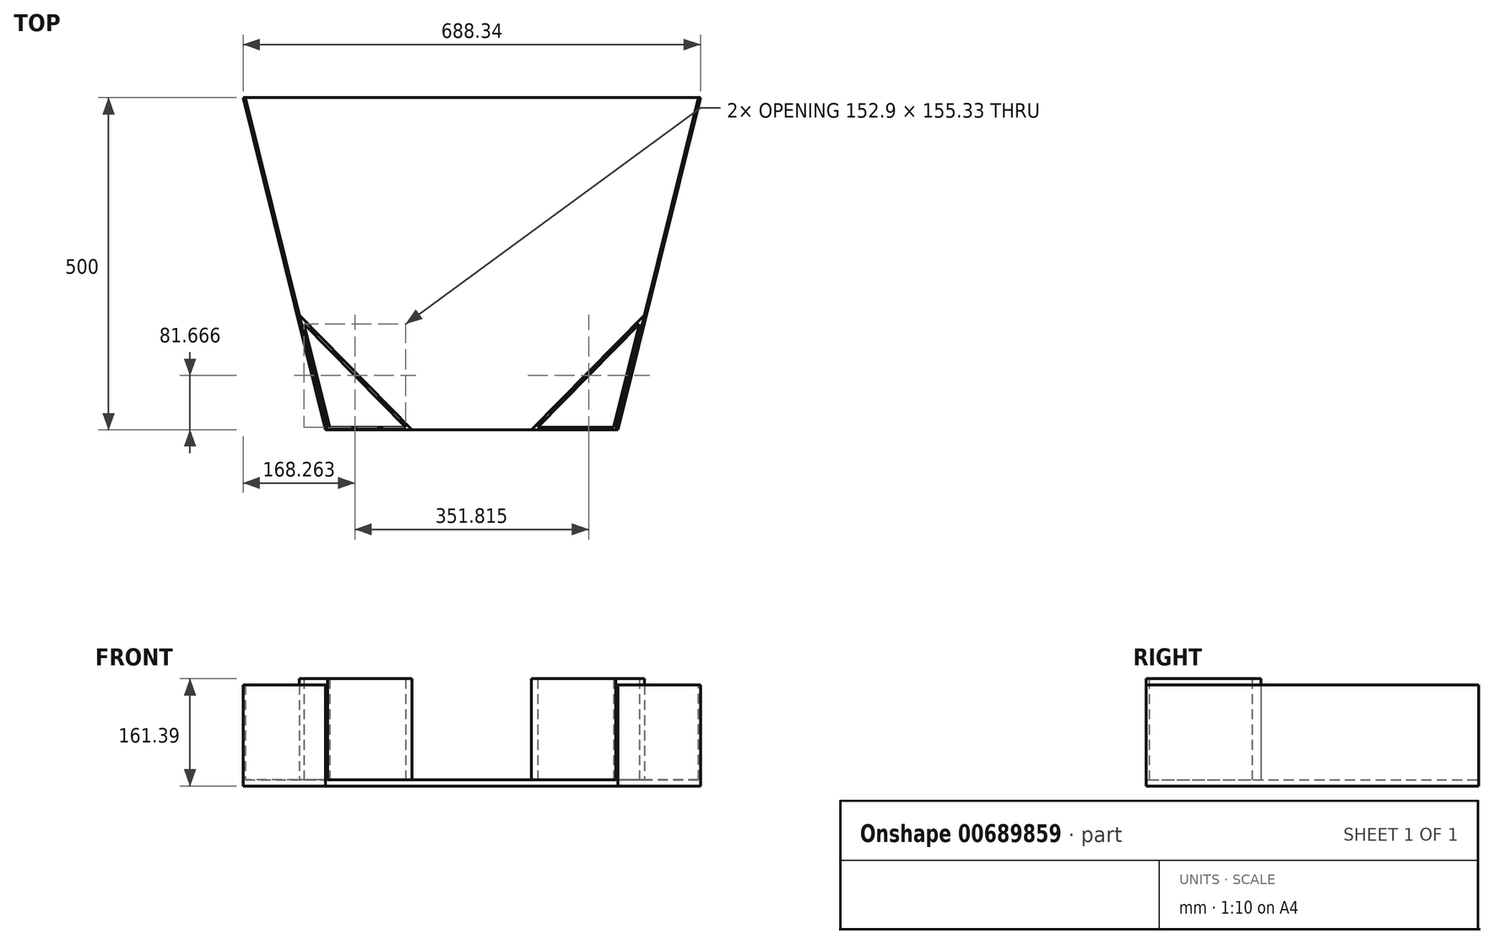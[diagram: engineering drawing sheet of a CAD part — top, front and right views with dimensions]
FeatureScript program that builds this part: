
annotation { "Feature Type Name" : "Feature", "Feature Type Description" : "" }
export const myFeature = defineFeature(function(context is Context, id is Id, definition is map)
    precondition{}
    {
        {
            var Q0;
            Q0=qCreatedBy(makeId("Top.planeOp"),FACE);
            var sketch = newSketch(context, id + "F0", { "sketchPlane" : qUnion([Q0])});
            skLineSegment(sketch, "E0", {"start": v(-344.17, 0) * mm, "end": v(344.17, 0) * mm});
            skLineSegment(sketch, "E1", {"start": v(344.17, 0) * mm, "end": v(220, -500) * mm});
            skLineSegment(sketch, "E2", {"start": v(220, -500) * mm, "end": v(-220, -500) * mm});
            skLineSegment(sketch, "E3", {"start": v(-220, -500) * mm, "end": v(-344.17, 0) * mm});
            skSolve(sketch);
        }
        {
            var Q0;
            Q0 = qSketchRegion(id + "F0", true);
            extrude(context, id + "F1", {"entities" : qUnion([Q0]), "depth" : 152.4 * mm, "offsetDistance" : 25.4 * mm});
        }
        {
            var Q0;
            Q0=makeQuery(id+"F1.opExtrude","CAP_FACE",FACE,{"disambiguationData":[OSD([sQuery(id+"F0.wireOp",EDGE,"E0"),sQuery(id+"F0.wireOp",EDGE,"E1"),sQuery(id+"F0.wireOp",EDGE,"E2"),sQuery(id+"F0.wireOp",EDGE,"E3")])],"isStart":false});
            var sketch = newSketch(context, id + "F2", { "sketchPlane" : qUnion([Q0])});
            skLineSegment(sketch, "E4.0", {"start": v(-216.9, -500) * mm, "end": v(-341.26, 0.72) * mm});
            skLineSegment(sketch, "E5.0", {"start": v(341.26, 0.72) * mm, "end": v(216.9, -500) * mm});
            skLineSegment(sketch, "E6", {"start": v(-341.26, 0.72) * mm, "end": v(341.26, 0.72) * mm});
            skLineSegment(sketch, "E7", {"start": v(-216.9, -500) * mm, "end": v(216.9, -500) * mm});
            skSolve(sketch);
        }
        {
            var Q0;
            Q0 = qSketchRegion(id + "F2", true);
            extrude(context, id + "F3", {"entities" : qUnion([Q0]), "operationType" : NewBodyOperationType.REMOVE, "oppositeDirection" : true, "depth" : 143.4 * mm, "offsetDistance" : 25.4 * mm});
        }
        {
            var Q0;
            Q0=makeQuery(id+"F3.boolean.opBoolean","COPY",FACE,{"derivedFrom":makeQuery(id+"F3.opExtrude","CAP_FACE",FACE,{"disambiguationData":[OSD([sQuery(id+"F2.wireOp",EDGE,"E4.0"),sQuery(id+"F2.wireOp",EDGE,"E5.0"),sQuery(id+"F2.wireOp",EDGE,"E6"),sQuery(id+"F2.wireOp",EDGE,"E7")])],"isStart":false})});
            var sketch = newSketch(context, id + "F4", { "sketchPlane" : qUnion([Q0])});
            skLineSegment(sketch, "E8", {"start": v(216.9, -500) * mm, "end": v(89.9, -500) * mm});
            skLineSegment(sketch, "E9", {"start": v(89.9, -500) * mm, "end": v(259.76, -327.44) * mm});
            skLineSegment(sketch, "E10", {"start": v(259.76, -327.44) * mm, "end": v(216.9, -500) * mm});
            skLineSegment(sketch, "E11", {"start": v(0, -500) * mm, "end": v(0, 0) * mm, "construction": true});
            skLineSegment(sketch, "E12.MirrorCS", {"start": v(-216.9, -500) * mm, "end": v(-89.9, -500) * mm});
            skLineSegment(sketch, "E13.MirrorCS", {"start": v(-259.76, -327.44) * mm, "end": v(-216.9, -500) * mm});
            skLineSegment(sketch, "E14.MirrorCS", {"start": v(-89.9, -500) * mm, "end": v(-259.76, -327.44) * mm});
            skLineSegment(sketch, "E15.0", {"start": v(99.46, -496) * mm, "end": v(252.36, -340.67) * mm});
            skLineSegment(sketch, "E15.1", {"start": v(213.78, -496) * mm, "end": v(99.46, -496) * mm});
            skLineSegment(sketch, "E15.2", {"start": v(252.36, -340.67) * mm, "end": v(213.78, -496) * mm});
            skLineSegment(sketch, "E16.0", {"start": v(-99.46, -496) * mm, "end": v(-252.36, -340.67) * mm});
            skLineSegment(sketch, "E16.1", {"start": v(-213.78, -496) * mm, "end": v(-99.46, -496) * mm});
            skLineSegment(sketch, "E16.2", {"start": v(-252.36, -340.67) * mm, "end": v(-213.78, -496) * mm});
            skSolve(sketch);
        }
        {
            var Q0;
            Q0 = qSketchRegion(id + "F4", true);
            extrude(context, id + "F5", {"entities" : qUnion([Q0]), "depth" : 152.4 * mm, "offsetDistance" : 25.4 * mm});
        }
    });
